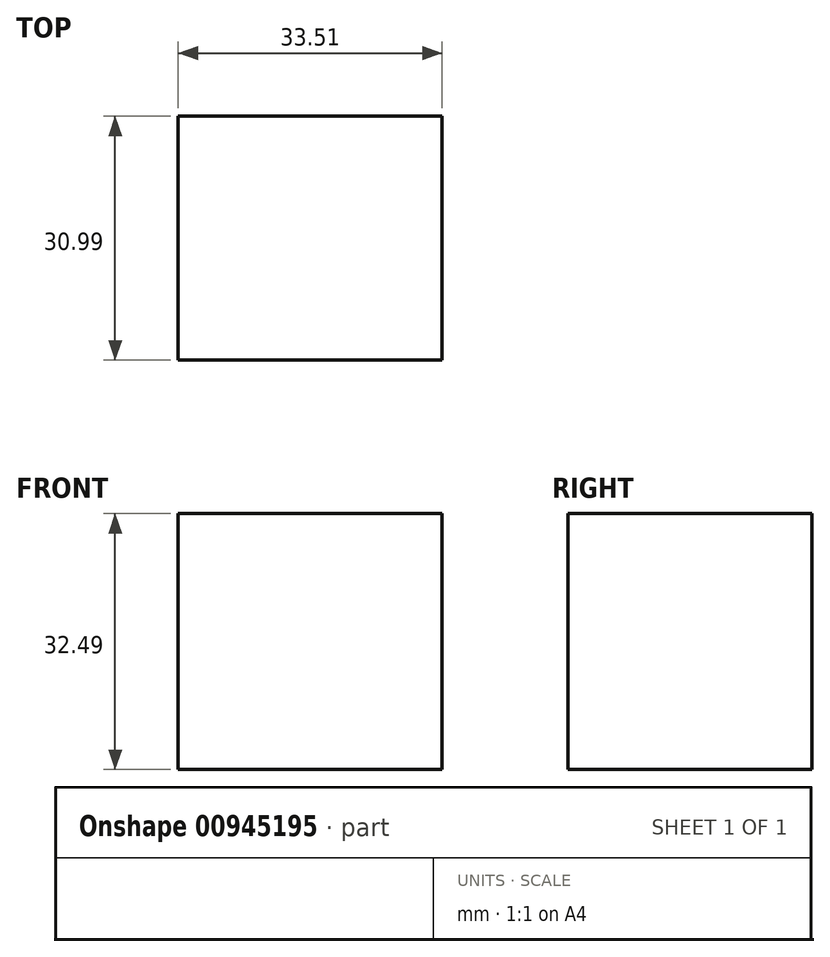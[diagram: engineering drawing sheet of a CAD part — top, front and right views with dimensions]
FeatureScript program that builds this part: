
annotation { "Feature Type Name" : "Feature", "Feature Type Description" : "" }
export const myFeature = defineFeature(function(context is Context, id is Id, definition is map)
    precondition{}
    {
        {
            var Q0;
            Q0=qCreatedBy(makeId("Front.planeOp"),FACE);
            var sketch = newSketch(context, id + "F0", { "sketchPlane" : qUnion([Q0])});
            skLineSegment(sketch, "E0", {"start": v(-21.1, 15.74) * mm, "end": v(-21.1, -15.74) * mm});
            skLineSegment(sketch, "E1", {"start": v(-21.1, -15.74) * mm, "end": v(12.42, -15.74) * mm});
            skLineSegment(sketch, "E2", {"start": v(12.42, -15.74) * mm, "end": v(12.42, 16.75) * mm});
            skLineSegment(sketch, "E3", {"start": v(12.42, 16.75) * mm, "end": v(-21.1, 16.75) * mm});
            skLineSegment(sketch, "E4", {"start": v(-21.1, 15.74) * mm, "end": v(-21.1, 16.75) * mm});
            skSolve(sketch);
        }
        {
            var Q0;
            Q0=makeQuery(id+"F0.imprint","IMPRINT",FACE,{"disambiguationData":[TD([[makeQuery(id+"F0.imprint","IMPRINT",EDGE,{"derivedFrom":sQuery(id+"F0.wireOp",EDGE,"E0")}),1.0]])]});
            extrude(context, id + "F1", {"entities" : qUnion([Q0]), "depth" : 30.99 * mm, "offsetDistance" : 25.4 * mm});
        }
        {
            var Q0;
            Q0=qCreatedBy(makeId("Front.planeOp"),FACE);
            var sketch = newSketch(context, id + "F2", { "sketchPlane" : qUnion([Q0])});
            skCircle(sketch, "E5", {"center": v(2.12, 8.88) * mm, "radius": 1.63 * mm});
            skCircle(sketch, "E6", {"center": v(-11, -6.26) * mm, "radius": 2.44 * mm});
            skSolve(sketch);
        }
        {
            var Q0;
            Q0=makeQuery(id+"F2.imprint","IMPRINT",FACE,{"disambiguationData":[TD([[makeQuery(id+"F2.imprint","IMPRINT",EDGE,{"derivedFrom":sQuery(id+"F2.wireOp",EDGE,"E6")}),1.0]])]});
            extrude(context, id + "F3", {"entities" : qUnion([Q0]), "operationType" : NewBodyOperationType.REMOVE, "oppositeDirection" : true, "depth" : 25.4 * mm, "offsetDistance" : 25.4 * mm});
        }
    });
